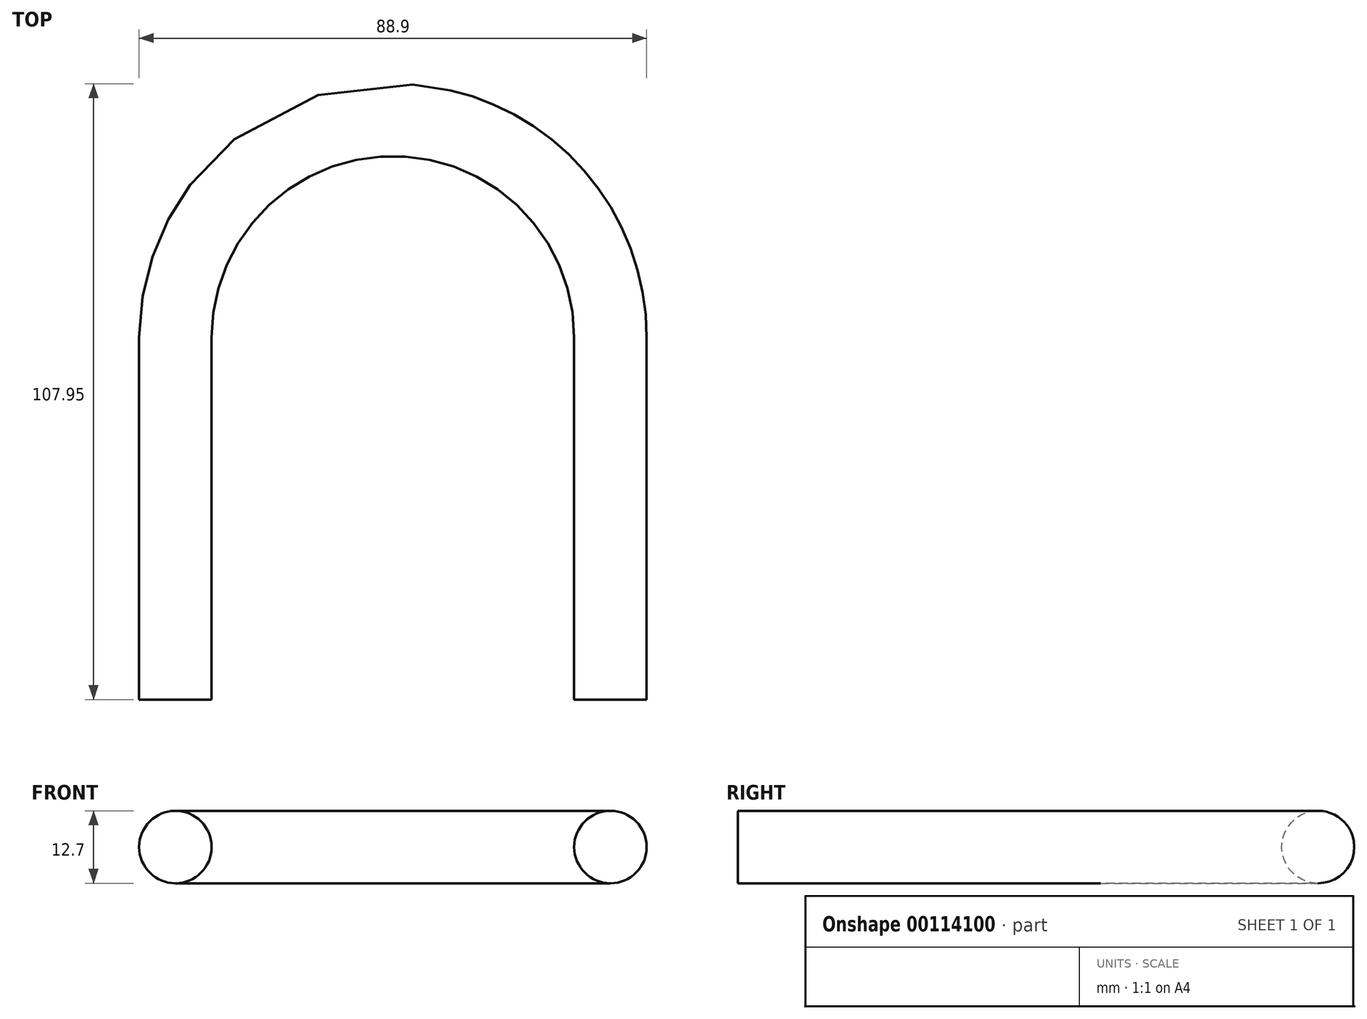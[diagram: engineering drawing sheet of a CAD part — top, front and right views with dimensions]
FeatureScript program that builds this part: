
annotation { "Feature Type Name" : "Feature", "Feature Type Description" : "" }
export const myFeature = defineFeature(function(context is Context, id is Id, definition is map)
    precondition{}
    {
        {
            var Q0;
            Q0=qCreatedBy(makeId("Top.planeOp"),FACE);
            var sketch = newSketch(context, id + "F0", { "sketchPlane" : qUnion([Q0])});
            skLineSegment(sketch, "E0", {"start": v(0, 0) * mm, "end": v(0, 63.5) * mm});
            skArc(sketch, "E1", {"start": v(0, 63.5) * mm, "mid": v(-38.1, 101.6) * mm, "end": v(-76.2, 63.5) * mm});
            skLineSegment(sketch, "E2", {"start": v(-76.2, 63.5) * mm, "end": v(-76.2, 0) * mm});
            skSolve(sketch);
        }
        {
            var Q0;
            Q0=qCreatedBy(makeId("Front.planeOp"),FACE);
            var sketch = newSketch(context, id + "F1", { "sketchPlane" : qUnion([Q0])});
            skCircle(sketch, "E3", {"center": v(0, 0) * mm, "radius": 6.35 * mm});
            skSolve(sketch);
        }
        {
            var Q0;
            Q0=makeQuery(id+"F1.imprint","IMPRINT",FACE,{"disambiguationData":[TD([[makeQuery(id+"F1.imprint","IMPRINT",EDGE,{"derivedFrom":sQuery(id+"F1.wireOp",EDGE,"E3")}),1.0]])]});
            var Q1;
            Q1 = qConstructionFilter(qBodyType(qCreatedBy(id + "F0" ,EDGE), BodyType.WIRE), ConstructionObject.NO);
            sweep(context, id + "F2", {"profiles" : qUnion([Q0]), "path" : qUnion([Q1])});
        }
    });
